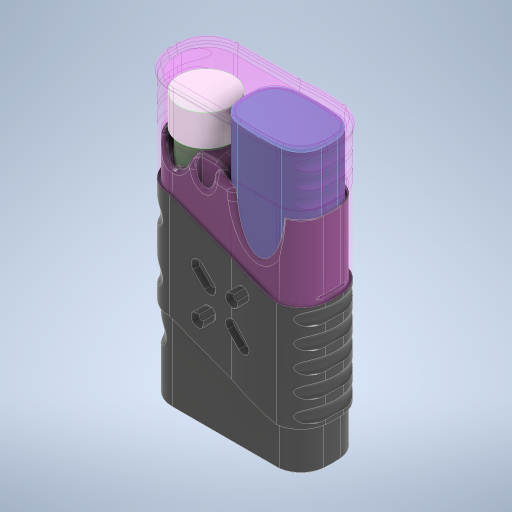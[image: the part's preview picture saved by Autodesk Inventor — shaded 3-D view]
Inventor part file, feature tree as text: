
AUTODESK INVENTOR PART (.ipt)
format: ipt  version: 2024.1 (Build 281209000, 209)  size: 3,916,288 bytes
history: native  units: mm
features: fillet x30, projected_geometry x28, extrude x27, sketch x13, other x6, revolve x6, sweep x2, pattern_circular x2, chamfer x2, plane x1, mirror x1
ambient origin geometry x8: Origin, YZ Plane, XZ Plane, XY Plane, X Axis, Y Axis, Z Axis, Center Point
bodies: Body1 (feature_tree), Body2 (feature_tree), Body3 (feature_tree), Body4 (feature_tree)
feature tree (118):
  other  "vape"
  extrude  "Extrusion1"  Depth=8.35mm
  fillet  "Fillet1"  Radius=80.0mm
  extrude  "Extrusion2"  Depth=11.6mm TaperAngle=0.0deg
  plane  "Work Plane1"
  extrude  "Extrusion3"  Depth=45.8mm TaperAngle=0.0deg
  extrude  "Extrusion4"  Depth=22.1mm
  extrude  "Extrusion5"  Depth=1.5mm
  extrude  "Extrusion6"  Depth=1.5mm
  fillet  "Fillet2"  Radius=1.5mm
  extrude  "Extrusion8"  Depth=15.55mm
  extrude  "Extrusion20"  Depth=3.0mm
  extrude  "Extrusion21"  Depth=3.0mm
  sweep  "Sweep2"
  extrude  "Extrusion22"  Depth=13.0mm
  fillet  "Fillet22"  Radius=2.0mm
  fillet  "Fillet23"  Radius=10.0mm
  fillet  "Fillet24"  Radius=11.0mm
  fillet  "Fillet25"  Radius=4.0mm
  fillet  "Fillet26"  Radius=2.0mm
  fillet  "Fillet4"  Radius=3.0mm
  extrude  "Extrusion10"  Depth=72.0mm TaperAngle=0.0deg
  extrude  "Extrusion11"  Depth=2.4mm
  fillet  "Fillet10"  Radius=7.3mm
  fillet  "Fillet27"  Radius=7.0mm
  extrude  "Extrusion13"  Depth=45.0mm TaperAngle=0.0deg
  fillet  "Fillet28"  Radius=0.25mm
  extrude  "Extrusion14"  Depth=71.0mm TaperAngle=0.0deg
  extrude  "Extrusion23"  Depth=71.0mm TaperAngle=0.0deg
  extrude  "Extrusion24"  Depth=3.0mm TaperAngle=30.0deg
  extrude  "Extrusion15"  Depth=1.0mm
  fillet  "Fillet29"  Radius=15.0mm
  extrude  "Extrusion25"  Depth=15.0mm TaperAngle=0.0deg
  fillet  "Fillet30"  [1 undecoded]
  other  "Work Axis1"
  sketch  "Sketch29"  dims[d28=17.0mm d29=45.8mm d30=0.0mm]
  revolve  "Revolution1"  [1 undecoded]
  sketch  "Sketch30"  dims[d31=17.0mm d38=22.1mm]
  revolve  "Revolution2"  [1 undecoded]
  fillet  "Fillet32"  Radius=15.780931mm
  extrude  "Extrusion26"  Depth=20.0mm
  revolve  "Revolution3"  [1 undecoded]
  revolve  "Revolution5"  [1 undecoded]
  extrude  "Extrusion27"  Depth=6.0mm
  extrude  "Extrusion28"  Depth=4.0mm
  fillet  "Fillet34"  Radius=1.0mm
  other  "Work Axis2"
  revolve  "Revolution6"  [1 undecoded]
  pattern_circular  "Circular Pattern1"  [2 undecoded]
  extrude  "Extrusion29"  Depth=0.5mm
  fillet  "Fillet35"  Radius=1.0mm
  fillet  "Fillet36"  Radius=24.0mm
  fillet  "Fillet37"  Radius=2.5mm
  fillet  "Fillet38"  Radius=0.7mm
  fillet  "Fillet39"  Radius=3.0mm
  fillet  "Fillet40"  Radius=5.0mm
  fillet  "Fillet41"  Radius=0.5mm
  pattern_circular  "Circular Pattern2"  [2 undecoded]
  fillet  "Fillet42"  Radius=10.0mm
  fillet  "Fillet43"  Radius=1.5mm
  fillet  "Fillet44"  Radius=6.0mm
  fillet  "Fillet45"  Radius=3.65mm
  fillet  "Fillet46"  Radius=10.0mm
  extrude  "Extrusion30"  Depth=2.5mm
  chamfer  "Chamfer2"  Distance=14.0mm
  mirror  "Mirror1"
  extrude  "Extrusion31"  Depth=19.0mm
  extrude  "Extrusion32"  TaperAngle=180.0deg  [1 undecoded]
  sketch  "Sketch48"  dims[d48=3.0mm d49=3.0mm]
  sweep  "Sweep3"
  revolve  "Revolution8"  [1 undecoded]
  fillet  "Fillet48"  Radius=7.8mm
  chamfer  "Chamfer3"  Distance=7.8mm
  extrude  "Extrusion33"  Depth=7.8mm
  extrude  "Extrusion34"  TaperAngle=0.0deg  [1 undecoded]
  fillet  "Fillet49"  [1 undecoded]
  fillet  "Fillet50"  Radius=1.5mm
  other  "vape-tube"
  other  "storage"
  projected_geometry  "Projected Loop2"
  projected_geometry  "Projected Loop3"
  projected_geometry  "Projected Loop4"
  projected_geometry  "Projected Loop6"
  other  "vape-lid"
  projected_geometry  "Projected Loop13"
  sketch  "Sketch23"  dims[d4=98.5mm d5=0.0mm d9=8.35mm d22=80.0mm d23=0.0mm]
  projected_geometry  "Projected Loop14"
  sketch  "Sketch25"  dims[d24=20.0mm d26=11.6mm d27=0.0mm]
  projected_geometry  "Projected Loop15"
  projected_geometry  "Projected Loop16"
  projected_geometry  "Projected Loop17"
  projected_geometry  "Projected Loop18"
  projected_geometry  "Projected Loop19"
  projected_geometry  "Projected Loop20"
  projected_geometry  "Projected Loop31"
  sketch  "Sketch37"  dims[d39=31.1mm d41=1.5mm]
  projected_geometry  "Projected Loop32"
  projected_geometry  "Projected Loop33"
  projected_geometry  "Projected Loop34"
  projected_geometry  "Projected Loop35"
  sketch  "Sketch45"  dims[d42=1.5mm d44=1.5mm d45=1.5mm]
  projected_geometry  "Projected Loop36"
  projected_geometry  "Projected Loop37"
  projected_geometry  "Projected Loop38"
  projected_geometry  "Projected Loop39"
  sketch  "Sketch47"  dims[d46=11.05mm d47=15.55mm]
  sketch  "Sketch49"  dims[d50=3.0mm d51=3.0mm]
  projected_geometry  "Projected Loop46"
  projected_geometry  "Projected Loop47"
  sketch  "3D Sketch1"
  projected_geometry  "Projected Loop48"
  projected_geometry  "Projected Loop49"
  projected_geometry  "Projected Loop50"
  projected_geometry  "Projected Loop51"
  sketch  "Sketch51"  dims[d52=11.05mm d53=15.55mm]
  sketch  "Sketch52"  dims[d54=2.0mm d55=13.0mm]
  projected_geometry  "Projected Loop53"
  sketch  "Sketch53"  dims[d56=12.5mm d57=60.0mm d58=0.0mm d59=2.0mm d60=10.0mm d61=0.0mm d62=11.0mm d66=4.0mm d67=0.0mm d69=2.0mm d83=3.0mm d86=72.0mm d87=0.0mm d88=2.4mm d89=7.3mm d91=7.0mm d92=45.0mm d93=0.0mm d94=0.25mm d105=71.0mm d106=0.0mm d108=71.0mm d109=0.0mm d110=3.0mm d111=30.0deg d158=1.0mm d159=15.0mm d160=0.0mm d161=15.0mm d162=0.0mm d163=0.0mm d164=0.0mm d169=0.0mm d170=0.0mm d171=15.0mm d172=15.780931mm d173=20.0mm d174=9.0mm d175=7.5mm d176=6.0mm d177=4.0mm d178=1.0mm d179=2.0mm d180=1.2mm d181=0.5mm d182=1.0mm d183=24.0mm d184=2.5mm d185=0.7mm d186=3.0mm d187=5.0mm d188=0.5mm d189=10.0mm d190=0.0mm d191=10.0mm d192=0.0mm d193=1.5mm d194=6.0mm d195=3.65mm d196=10.0mm d197=0.0mm d198=2.5mm d199=14.0mm d200=19.0mm d201=19.0mm d207=180.0deg d208=7.8mm d209=8.0mm d210=7.8mm d211=7.8mm d212=7.8mm d215=0.0mm d216=180.0deg d218=1.5mm d220=0.5mm d221=18.25mm d222=0.0mm d225=6.0mm d226=6.0mm d227=11.5mm d228=6.0mm d229=6.0mm d230=180.0deg d240=3.0mm d241=6.0mm d242=6.0mm d243=6.0mm d244=41.5mm d245=11.5mm d246=6.0mm d247=180.0deg d249=20.0mm d253=22.0mm d254=22.0mm d255=25.0mm d256=1.0mm d257=1.0mm d258=0.0mm d259=1.0mm d260=0.0mm d261=0.2mm d263=5.0mm d264=10.0mm d265=2.241222mm d266=10.0mm d267=30.0mm d268=4.0mm d269=45.0deg d270=40.0mm d271=360.0deg d275=0.4mm d276=1.1mm d277=2.4mm d278=3.0mm d279=1.5mm d280=3.0mm d281=0.810487mm d282=2.943591mm d283=4.5mm d284=0.0mm d285=2.0mm d286=0.8mm d287=3.0mm d288=0.5mm d289=1.0mm d290=1.0mm d291=1.0mm d292=40.0mm d293=360.0deg d295=1.0mm d296=0.5mm d297=0.5mm d298=1.0mm d299=0.4mm d312=12.0mm d315=8.5mm d316=8.5mm d317=5.0mm d318=40.0mm d320=360.0deg d322=10.0mm d323=1.5mm d324=0.0mm d325=0.0mm d329=1.5mm d330=2.0mm d331=45.0deg d332=21.0mm d334=5.458726mm d335=19.0mm d336=30.0mm d337=42.5mm d338=30.0mm d339=0.0mm d340=15.0mm d341=0.0mm d342=0.0mm d343=0.0mm d344=29.760104mm d349=22.0mm d350=24.0mm d351=180.0deg d352=2.0mm d353=0.5mm d354=15.0mm d355=45.0deg d365=1.5mm d366=1.5mm d367=15.0mm d368=0.0mm d369=1.5mm d370=0.25mm d371=0.25mm d372=1.4mm d373=1.5mm d374=1.5mm d375=7.5mm d376=0.0mm d377=0.4mm d378=0.4mm]
note: 14 required parameter values undecoded (feature->parameter linkage not recoverable at this tier; creation-order binding heuristic only, values carry confidence <= 0.55)